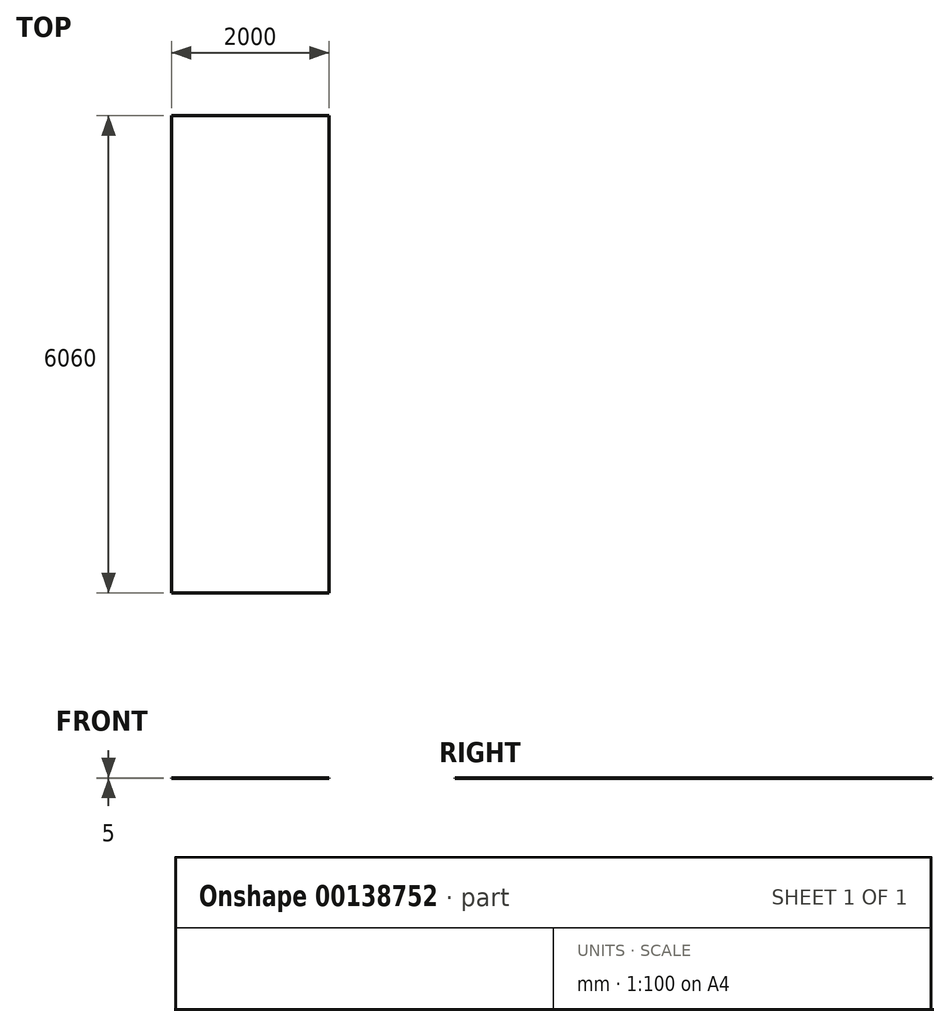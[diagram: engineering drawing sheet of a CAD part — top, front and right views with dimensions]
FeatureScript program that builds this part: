
annotation { "Feature Type Name" : "Feature", "Feature Type Description" : "" }
export const myFeature = defineFeature(function(context is Context, id is Id, definition is map)
    precondition{}
    {
        {
            var Q0;
            Q0=qCreatedBy(makeId("Front.planeOp"),FACE);
            var sketch = newSketch(context, id + "F0", { "sketchPlane" : qUnion([Q0])});
            skLineSegment(sketch, "E0.bottom", {"start": v(-988.5, -53.05) * mm, "end": v(1011.5, -53.05) * mm});
            skLineSegment(sketch, "E0.top", {"start": v(-988.5, -58.05) * mm, "end": v(1011.5, -58.05) * mm});
            skLineSegment(sketch, "E0.left", {"start": v(-988.5, -53.05) * mm, "end": v(-988.5, -58.05) * mm});
            skLineSegment(sketch, "E0.right", {"start": v(1011.5, -53.05) * mm, "end": v(1011.5, -58.05) * mm});
            skSolve(sketch);
        }
        {
            var Q0;
            Q0=qSketchRegion(id+"F0",true);
            extrude(context, id + "F1", {"entities" : qUnion([Q0]), "endBound" : BoundingType.SYMMETRIC, "depth" : 6060 * mm});
        }
    });
